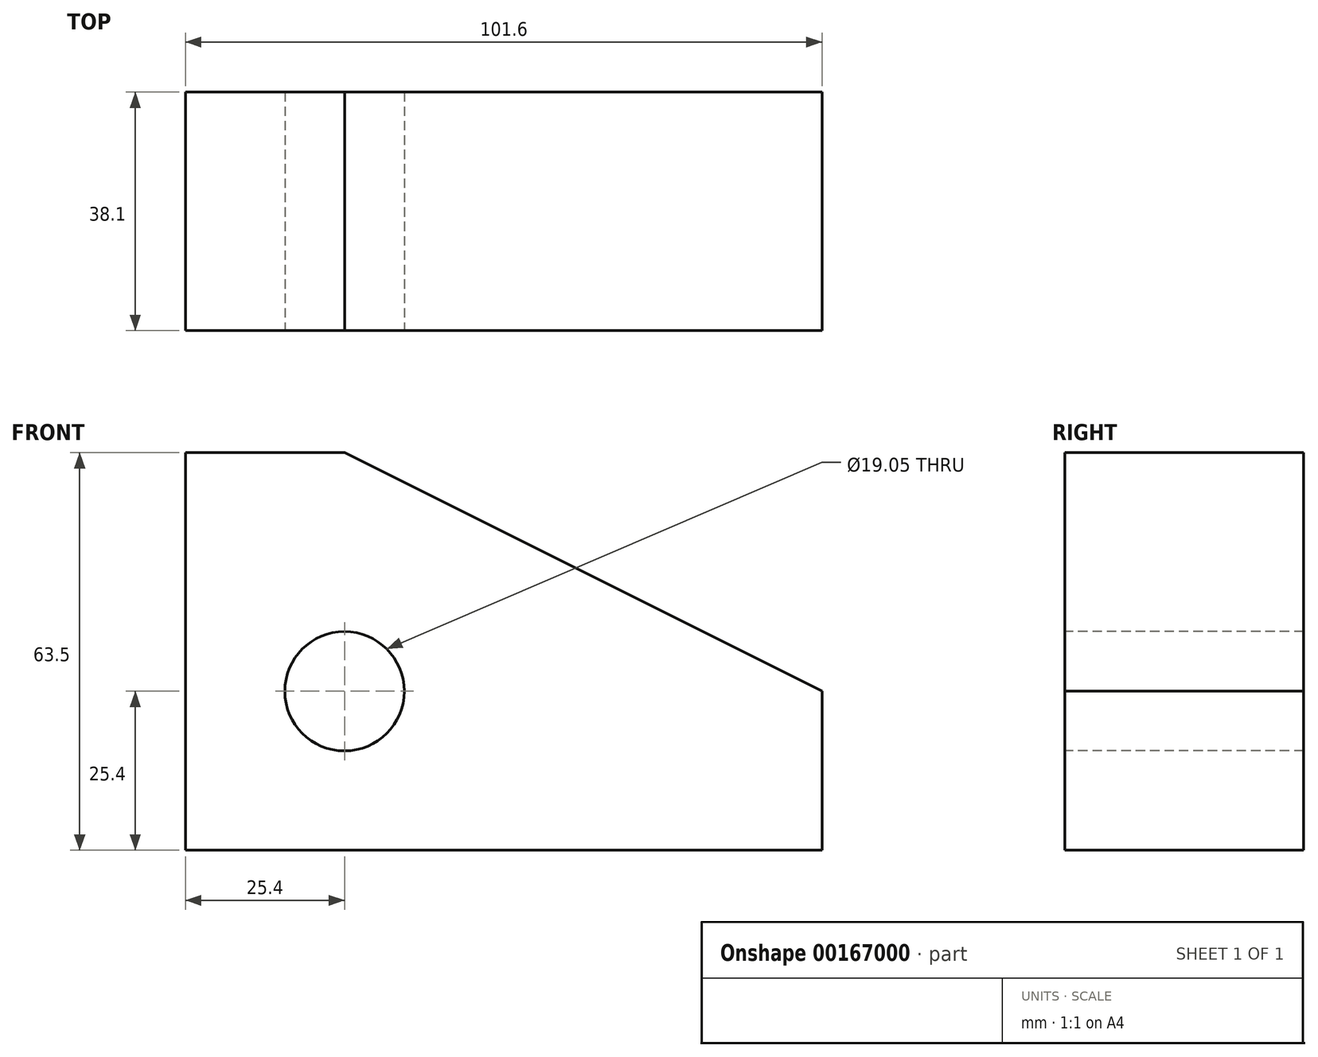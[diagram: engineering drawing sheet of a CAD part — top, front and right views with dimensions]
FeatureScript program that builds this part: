
annotation { "Feature Type Name" : "Feature", "Feature Type Description" : "" }
export const myFeature = defineFeature(function(context is Context, id is Id, definition is map)
    precondition{}
    {
        {
            var Q0;
            Q0=qCreatedBy(makeId("Front.planeOp"),FACE);
            var sketch = newSketch(context, id + "F0", { "sketchPlane" : qUnion([Q0])});
            skLineSegment(sketch, "E0", {"start": v(0, 0) * mm, "end": v(101.6, 0) * mm});
            skLineSegment(sketch, "E1", {"start": v(101.6, 0) * mm, "end": v(101.6, 25.4) * mm});
            skLineSegment(sketch, "E2", {"start": v(101.6, 25.4) * mm, "end": v(25.4, 63.5) * mm});
            skLineSegment(sketch, "E3", {"start": v(25.4, 63.5) * mm, "end": v(0, 63.5) * mm});
            skLineSegment(sketch, "E4", {"start": v(0, 63.5) * mm, "end": v(0, 0) * mm});
            skSolve(sketch);
        }
        {
            var Q0;
            Q0=makeQuery(id+"F0.imprint","IMPRINT",FACE,{"disambiguationData":[TD([[makeQuery(id+"F0.imprint","IMPRINT",EDGE,{"derivedFrom":sQuery(id+"F0.wireOp",EDGE,"E0")}),1.0]])]});
            extrude(context, id + "F1", {"entities" : qUnion([Q0]), "depth" : 38.1 * mm});
        }
        {
            var Q0;
            Q0=makeQuery(id+"F1.opExtrude","CAP_FACE",FACE,{"disambiguationData":[OSD([sQuery(id+"F0.wireOp",EDGE,"E0"),sQuery(id+"F0.wireOp",EDGE,"E1"),sQuery(id+"F0.wireOp",EDGE,"E2"),sQuery(id+"F0.wireOp",EDGE,"E3"),sQuery(id+"F0.wireOp",EDGE,"E4")])],"isStart":false});
            var sketch = newSketch(context, id + "F2", { "sketchPlane" : qUnion([Q0])});
            skCircle(sketch, "E5", {"center": v(25.4, 25.4) * mm, "radius": 9.53 * mm});
            skSolve(sketch);
        }
        {
            var Q0;
            Q0=makeQuery(id+"F2.imprint","IMPRINT",FACE,{"disambiguationData":[TD([[makeQuery(id+"F2.imprint","IMPRINT",EDGE,{"derivedFrom":sQuery(id+"F2.wireOp",EDGE,"E5")}),1.0]])]});
            extrude(context, id + "F3", {"entities" : qUnion([Q0]), "operationType" : NewBodyOperationType.REMOVE, "endBound" : BoundingType.THROUGH_ALL, "oppositeDirection" : true, "depth" : 25.4 * mm});
        }
    });
